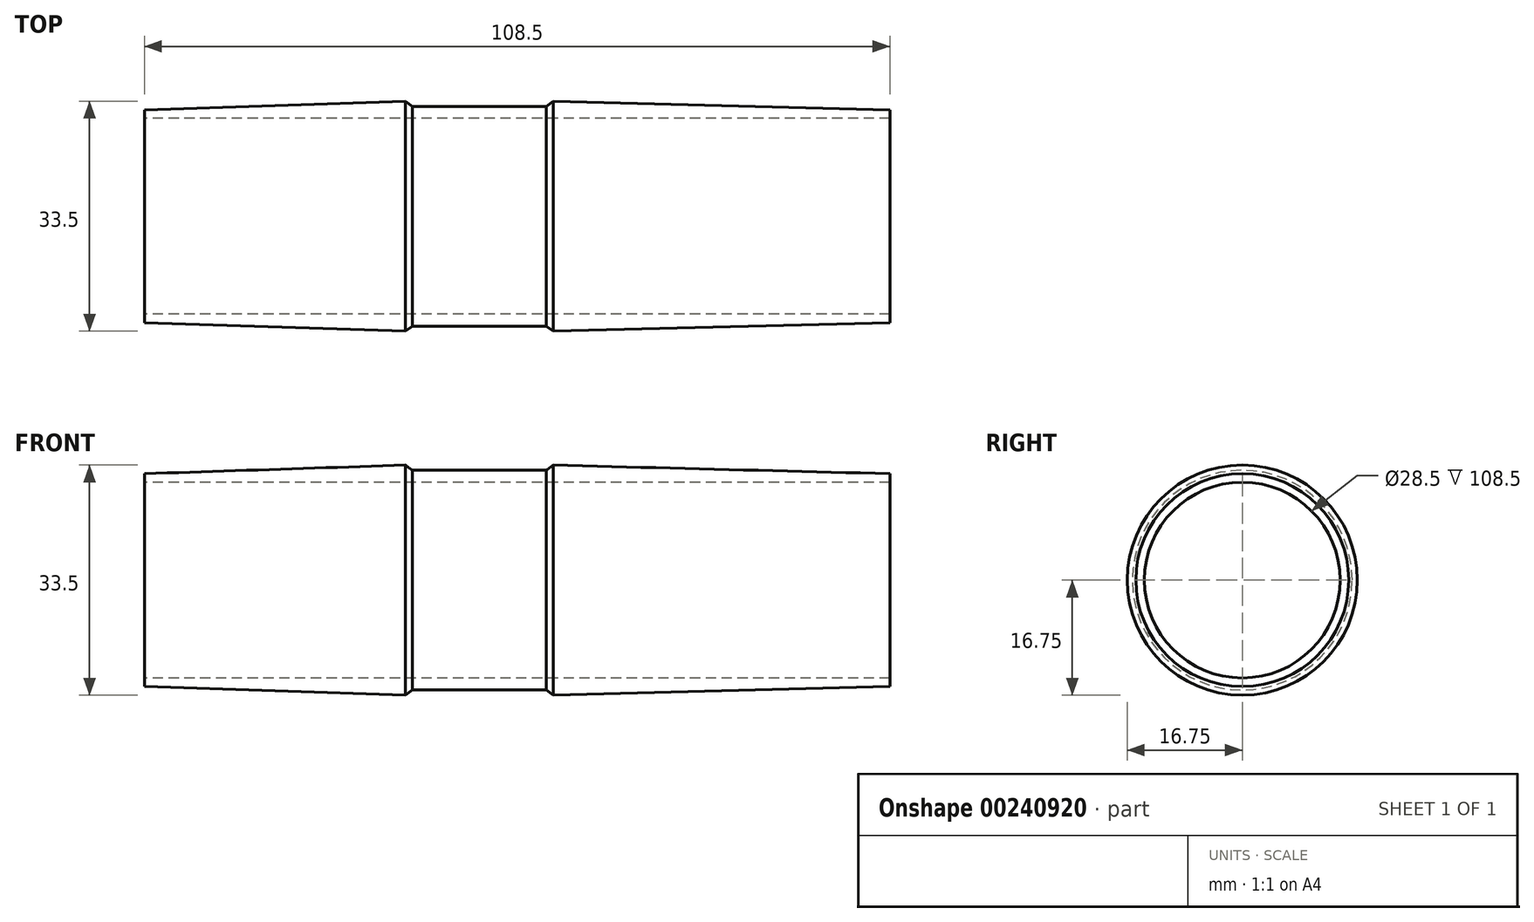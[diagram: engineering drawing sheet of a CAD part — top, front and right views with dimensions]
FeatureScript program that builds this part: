
annotation { "Feature Type Name" : "Feature", "Feature Type Description" : "" }
export const myFeature = defineFeature(function(context is Context, id is Id, definition is map)
    precondition{}
    {
        {
            var Q0;
            Q0=qCreatedBy(makeId("Front.planeOp"),FACE);
            var sketch = newSketch(context, id + "F0", { "sketchPlane" : qUnion([Q0])});
            skLineSegment(sketch, "E0", {"start": v(-54, 14.25) * mm, "end": v(54.5, 14.25) * mm});
            skLineSegment(sketch, "E1", {"start": v(-54, 14.25) * mm, "end": v(-54, 15.5) * mm});
            skLineSegment(sketch, "E2", {"start": v(-54, 15.5) * mm, "end": v(-16, 16.75) * mm});
            skLineSegment(sketch, "E3", {"start": v(-16, 16.75) * mm, "end": v(-15.03, 16) * mm});
            skLineSegment(sketch, "E4", {"start": v(-15.03, 16) * mm, "end": v(4.47, 16) * mm});
            skLineSegment(sketch, "E5", {"start": v(54.5, 14.25) * mm, "end": v(54.5, 15.5) * mm});
            skLineSegment(sketch, "E6", {"start": v(54.5, 15.5) * mm, "end": v(5.5, 16.75) * mm});
            skLineSegment(sketch, "E7", {"start": v(5.5, 16.75) * mm, "end": v(4.47, 16) * mm});
            skSolve(sketch);
        }
        {
            var Q0;
            Q0=qCreatedBy(makeId("Front.planeOp"),FACE);
            var sketch = newSketch(context, id + "F1", { "sketchPlane" : qUnion([Q0])});
            skLineSegment(sketch, "E8", {"start": v(-74.63, 0) * mm, "end": v(72.24, 0) * mm});
            skSolve(sketch);
        }
        {
            var Q0;
            Q0=makeQuery(id+"F0.imprint","IMPRINT",FACE,{"disambiguationData":[TD([[makeQuery(id+"F0.imprint","IMPRINT",EDGE,{"derivedFrom":sQuery(id+"F0.wireOp",EDGE,"E0")}),1.0]])]});
            var Q1;
            Q1=sQuery(id+"F1.wireOp",EDGE,"E8");
            revolve(context, id + "F2", {"entities" : qUnion([Q0]), "axis" : qUnion([Q1]), "revolveType" : RevolveType.FULL});
        }
    });
